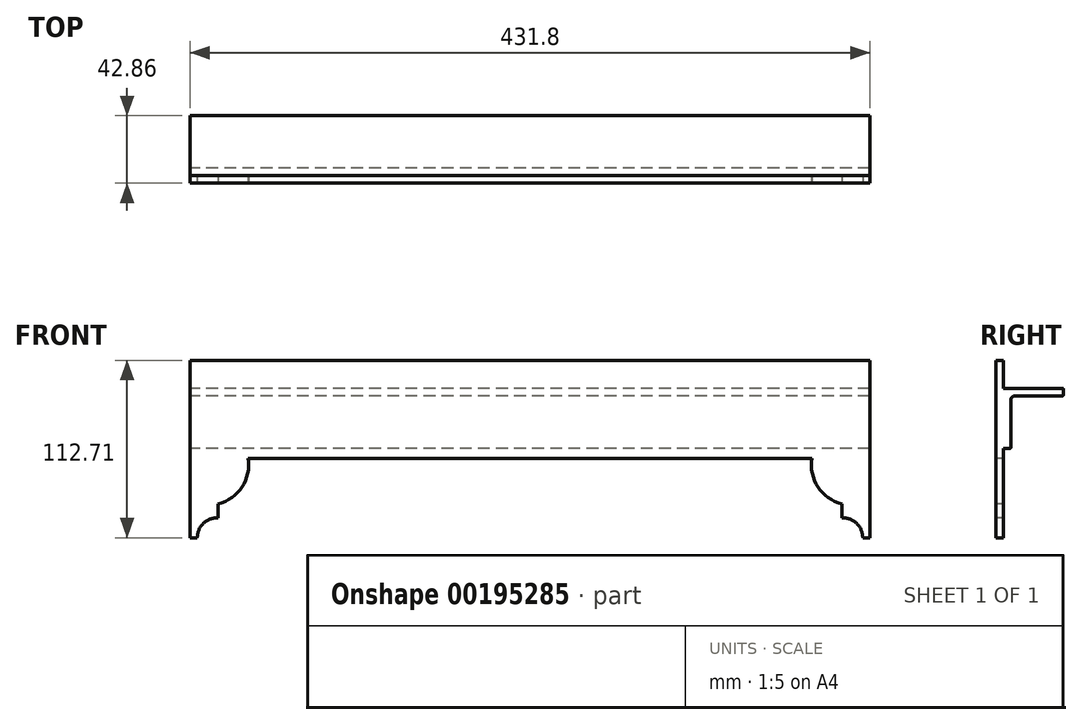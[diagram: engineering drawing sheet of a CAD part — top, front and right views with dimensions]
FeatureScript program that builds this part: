
annotation { "Feature Type Name" : "Feature", "Feature Type Description" : "" }
export const myFeature = defineFeature(function(context is Context, id is Id, definition is map)
    precondition{}
    {
        {
            var Q0;
            Q0=qCreatedBy(makeId("Front.planeOp"),FACE);
            var sketch = newSketch(context, id + "F0", { "sketchPlane" : qUnion([Q0])});
            skLineSegment(sketch, "E0", {"start": v(-215.9, 0) * mm, "end": v(-431.8, 0) * mm});
            skLineSegment(sketch, "E1", {"start": v(-431.8, 0) * mm, "end": v(-431.8, -112.71) * mm});
            skLineSegment(sketch, "E2", {"start": v(-431.8, -112.71) * mm, "end": v(-427.23, -112.71) * mm});
            skLineSegment(sketch, "E3", {"start": v(-394.97, -62.23) * mm, "end": v(-215.9, -62.23) * mm});
            skArc(sketch, "E4", {"start": v(-414.02, -100.02) * mm, "mid": v(-423.33, -103.55) * mm, "end": v(-427.23, -112.71) * mm});
            skLineSegment(sketch, "E5", {"start": v(-414.02, -100.02) * mm, "end": v(-414.02, -91.13) * mm});
            skArc(sketch, "E6", {"start": v(-414.02, -91.13) * mm, "mid": v(-398.8, -80.43) * mm, "end": v(-394.97, -62.23) * mm});
            skLineSegment(sketch, "E7", {"start": v(-215.9, 0) * mm, "end": v(-215.9, -62.23) * mm, "construction": true});
            skPoint(sketch, "E8.end.orphan", {"position": v(0, 0) * mm});
            skPoint(sketch, "E9.trimOffspring.end.orphan", {"position": v(0, -112.71) * mm});
            skPoint(sketch, "E10.orphan", {"position": v(-36.83, -62.23) * mm});
            skPoint(sketch, "E11.center.orphan", {"position": v(-17.27, -112.71) * mm});
            skLineSegment(sketch, "E12.MirrorCS", {"start": v(-17.78, -100.02) * mm, "end": v(-17.78, -91.13) * mm});
            skLineSegment(sketch, "E13.MirrorCS", {"start": v(-36.83, -62.23) * mm, "end": v(-215.9, -62.23) * mm});
            skArc(sketch, "E14.MirrorCS", {"start": v(-17.78, -91.13) * mm, "mid": v(-33, -80.43) * mm, "end": v(-36.83, -62.23) * mm});
            skArc(sketch, "E15.MirrorCS", {"start": v(-17.78, -100.02) * mm, "mid": v(-8.47, -103.55) * mm, "end": v(-4.57, -112.71) * mm});
            skLineSegment(sketch, "E16.MirrorCS", {"start": v(0, 0) * mm, "end": v(0, -112.71) * mm});
            skLineSegment(sketch, "E17.MirrorCS", {"start": v(-215.9, 0) * mm, "end": v(0, 0) * mm});
            skLineSegment(sketch, "E18.MirrorCS", {"start": v(0, -112.71) * mm, "end": v(-4.57, -112.71) * mm});
            skPoint(sketch, "E19.orphan", {"position": v(-401.83, -112.71) * mm});
            skPoint(sketch, "E20.orphan", {"position": v(-29.97, -112.71) * mm});
            skSolve(sketch);
        }
        {
            var Q0;
            Q0=makeQuery(id+"F0.imprint","IMPRINT",FACE,{"disambiguationData":[TD([[makeQuery(id+"F0.imprint","IMPRINT",EDGE,{"derivedFrom":sQuery(id+"F0.wireOp",EDGE,"E0")}),1.0]])]});
            extrude(context, id + "F1", {"entities" : qUnion([Q0]), "oppositeDirection" : true, "depth" : 4.76 * mm});
        }
        {
            var Q0;
            Q0=makeQuery(id+"F1.opExtrude","SWEPT_FACE",FACE,{"disambiguationData":[OSD([sQuery(id+"F0.wireOp",EDGE,"E1")])]});
            var sketch = newSketch(context, id + "F2", { "sketchPlane" : qUnion([Q0])});
            skLineSegment(sketch, "E21", {"start": v(-4.76, -17.78) * mm, "end": v(-42.35, -17.78) * mm});
            skLineSegment(sketch, "E22", {"start": v(-42.86, -18.29) * mm, "end": v(-42.86, -22.03) * mm});
            skLineSegment(sketch, "E23", {"start": v(-42.35, -22.54) * mm, "end": v(-12.08, -22.54) * mm});
            skLineSegment(sketch, "E24", {"start": v(-9.54, -25.08) * mm, "end": v(-9.54, -55.37) * mm});
            skLineSegment(sketch, "E25", {"start": v(-9.03, -55.88) * mm, "end": v(-4.76, -55.88) * mm});
            skPoint(sketch, "E26.visualSharp", {"position": v(-9.54, -22.54) * mm});
            skArc(sketch, "E26.filletArc", {"start": v(-9.54, -25.08) * mm, "mid": v(-10.28, -23.29) * mm, "end": v(-12.08, -22.54) * mm});
            skPoint(sketch, "E27.visualSharp", {"position": v(-42.86, -17.78) * mm});
            skArc(sketch, "E27.filletArc", {"start": v(-42.35, -17.78) * mm, "mid": v(-42.71, -17.93) * mm, "end": v(-42.86, -18.29) * mm});
            skPoint(sketch, "E28.visualSharp", {"position": v(-42.86, -22.54) * mm});
            skArc(sketch, "E28.filletArc", {"start": v(-42.86, -22.03) * mm, "mid": v(-42.71, -22.4) * mm, "end": v(-42.35, -22.54) * mm});
            skPoint(sketch, "E29.visualSharp", {"position": v(-9.54, -55.88) * mm});
            skArc(sketch, "E29.filletArc", {"start": v(-9.54, -55.37) * mm, "mid": v(-9.39, -55.73) * mm, "end": v(-9.03, -55.88) * mm});
            skSolve(sketch);
        }
        {
            var Q0;
            {var subQ0=sQuery(id+"F2.wireOp",EDGE,"E21");Q0=makeQuery(id+"F2.imprint","IMPRINT",FACE,{"disambiguationData":[TD([[makeQuery(id+"F2.imprint","IMPRINT",EDGE,{"derivedFrom":subQ0}),1.0]])]});}
            var Q1;
            Q1=makeQuery(id+"F1.opExtrude","SWEPT_FACE",FACE,{"disambiguationData":[OSD([sQuery(id+"F0.wireOp",EDGE,"E16.MirrorCS")])]});
            extrude(context, id + "F3", {"entities" : qUnion([Q0]), "operationType" : NewBodyOperationType.ADD, "endBound" : BoundingType.UP_TO_SURFACE, "oppositeDirection" : true, "endBoundEntityFace" : qUnion([Q1]), "depth" : 442.91 * mm});
        }
    });
